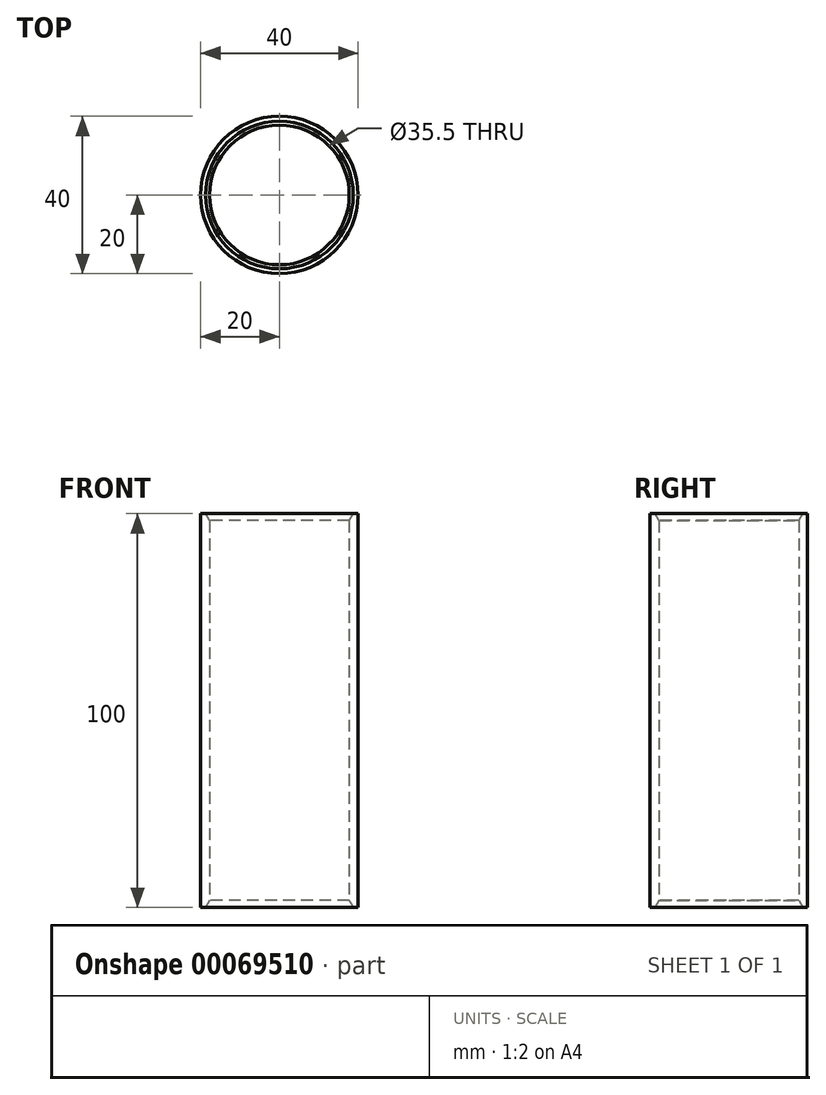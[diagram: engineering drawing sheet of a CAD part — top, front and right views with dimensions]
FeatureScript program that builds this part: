
annotation { "Feature Type Name" : "Feature", "Feature Type Description" : "" }
export const myFeature = defineFeature(function(context is Context, id is Id, definition is map)
    precondition{}
    {
        {
            var Q0;
            Q0=qCreatedBy(makeId("Top.planeOp"),FACE);
            var sketch = newSketch(context, id + "F0", { "sketchPlane" : qUnion([Q0])});
            skCircle(sketch, "E0", {"center": v(0, 0) * mm, "radius": 17.75 * mm});
            skCircle(sketch, "E1", {"center": v(0, 0) * mm, "radius": 20 * mm});
            skSolve(sketch);
        }
        {
            var Q0;
            Q0=makeQuery(id+"F0.imprint","IMPRINT",FACE,{"disambiguationData":[TD([[makeQuery(id+"F0.imprint","IMPRINT",EDGE,{"derivedFrom":sQuery(id+"F0.wireOp",EDGE,"E0")}),-1.0]])]});
            extrude(context, id + "F1", {"entities" : qUnion([Q0]), "depth" : 100 * mm});
        }
        {
            var Q0;
            Q0=makeQuery(id+"F1.opExtrude","CAP_EDGE",EDGE,{"disambiguationData":[OSD([sQuery(id+"F0.wireOp",EDGE,"E0")])],"isStart":false});
            var Q1;
            Q1=makeQuery(id+"F1.opExtrude","CAP_EDGE",EDGE,{"disambiguationData":[OSD([sQuery(id+"F0.wireOp",EDGE,"E0")])],"isStart":true});
            chamfer(context, id + "F2", {"entities" : qUnion([Q0, Q1]), "chamferType" : ChamferType.OFFSET_ANGLE, "width" : 1 * mm, "oppositeDirection" : true, "angle" : 60 * degree, "tangentPropagation" : true});
        }
    });
